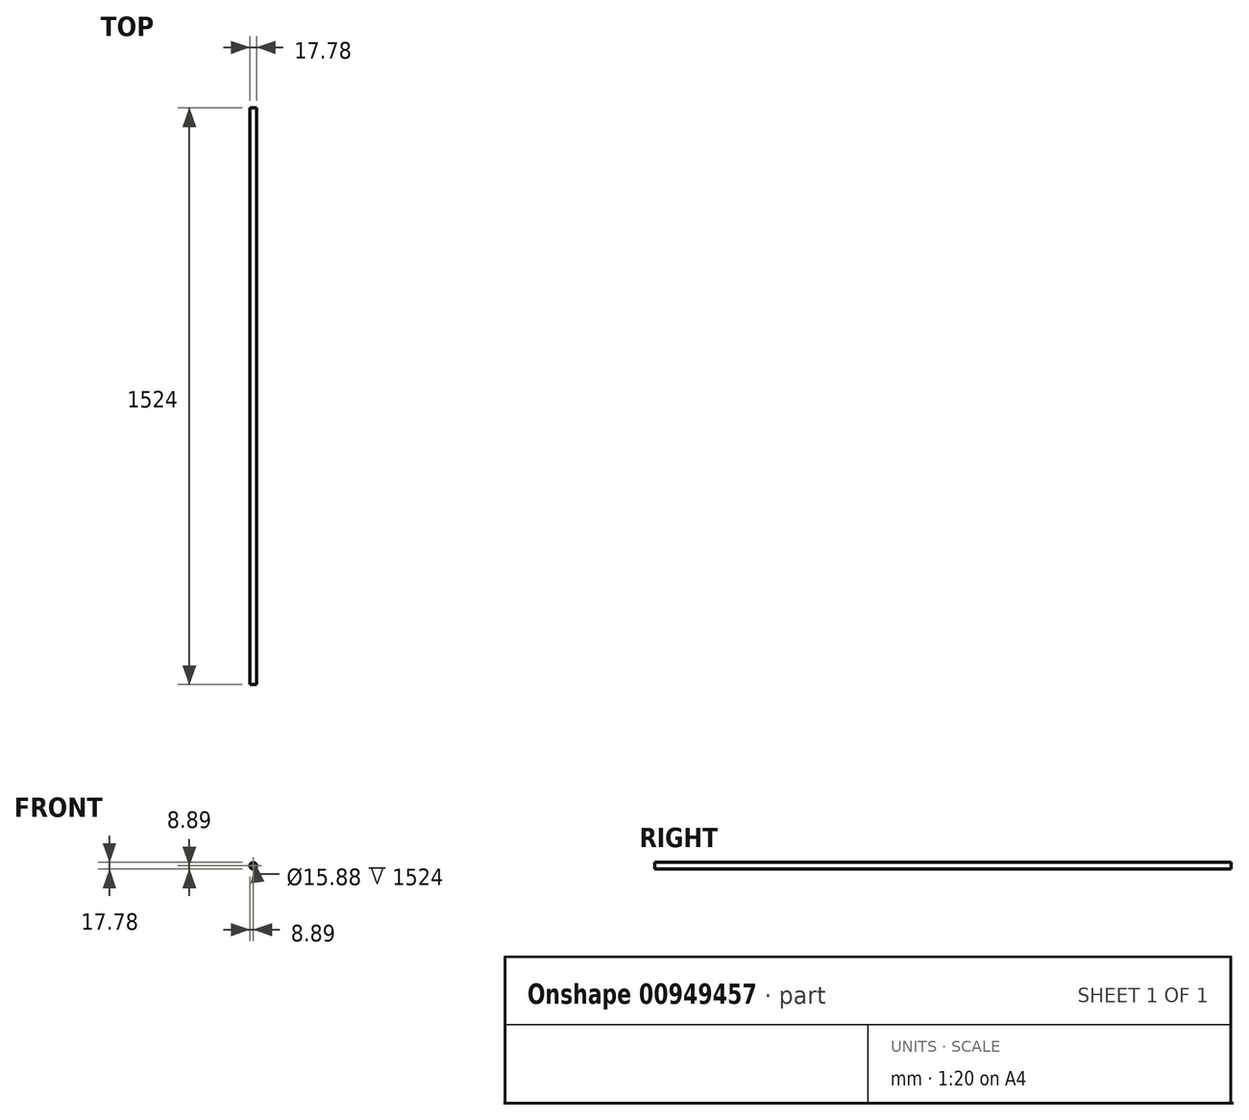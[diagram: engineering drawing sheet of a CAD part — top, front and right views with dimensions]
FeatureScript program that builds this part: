
annotation { "Feature Type Name" : "Feature", "Feature Type Description" : "" }
export const myFeature = defineFeature(function(context is Context, id is Id, definition is map)
    precondition{}
    {
        {
            var Q0;
            Q0=qCreatedBy(makeId("Front.planeOp"),FACE);
            var sketch = newSketch(context, id + "F0", { "sketchPlane" : qUnion([Q0])});
            skCircle(sketch, "E0", {"center": v(0, 0) * mm, "radius": 8.9 * mm});
            skCircle(sketch, "E1", {"center": v(0, 0) * mm, "radius": 7.94 * mm});
            skSolve(sketch);
        }
        {
            var Q0;
            Q0=makeQuery(id+"F0.imprint","IMPRINT",FACE,{"disambiguationData":[TD([[makeQuery(id+"F0.imprint","IMPRINT",EDGE,{"derivedFrom":sQuery(id+"F0.wireOp",EDGE,"E0")}),1.0]])]});
            extrude(context, id + "F1", {"entities" : qUnion([Q0]), "depth" : 1524 * mm, "offsetDistance" : 25.4 * mm});
        }
    });
